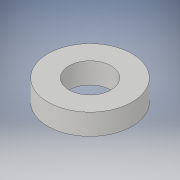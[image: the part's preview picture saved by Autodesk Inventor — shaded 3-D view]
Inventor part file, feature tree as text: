
AUTODESK INVENTOR PART (.ipt)
format: ipt  version: 2017 (Build 210142000, 142)  size: 96,256 bytes
history: native  units: in
note: dims shown in document units (in); Inventor stores cm internally (conversion verified against a paired STEP export)
features: extrude x1, sketch x1
ambient origin geometry x8: Origin, YZ Plane, XZ Plane, XY Plane, X Axis, Y Axis, Z Axis, Center Point
bodies: Solid1 (feature_tree)
feature tree (2):
  extrude  "Extrusion1"  Depth=0.125in
  sketch  "Sketch1"  dims[d0=0.25in d1=0.5in d2=0.125in d3=0.0in]
